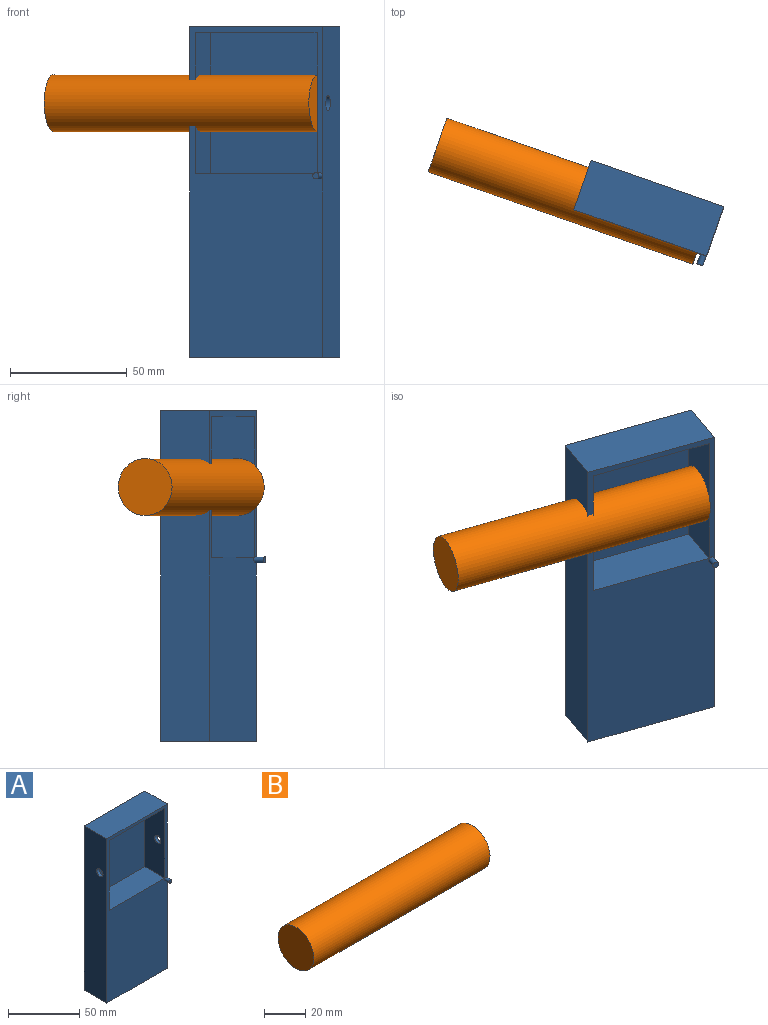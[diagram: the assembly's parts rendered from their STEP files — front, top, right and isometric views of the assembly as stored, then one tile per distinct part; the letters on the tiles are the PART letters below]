
ASSEMBLY  parts=2 mates=1
PART A: 43 faces, bbox 60.3x26.8x141.5 mm
  f0: plane 141.5x60.26mm, normal (0,-1,0), area 5197.6mm2, adj f1,f2,f3,f5,f6,f7,f8,f12
  f1: plane 141.5x22.41mm, normal (1,0,0), area 3139.2mm2, adj f0,f2,f4,f11,f39
  f2: plane 60.26x22.41mm, normal (0,0,1), area 1350.3mm2, adj f0,f1,f3,f4
  f3: plane 141.5x22.41mm, normal (-1,0,0), area 3139.2mm2, adj f0,f2,f4,f10,f39
  f4: plane 141.5x60.26mm, normal (0,1,0), area 8526.4mm2, adj f1,f2,f3,f39
  f5: plane 60.22x19.87mm, normal (-1,0,0), area 1164.8mm2, adj f0,f6,f8,f9,f11
  f6: plane 55.18x19.87mm, normal (0,0,-1), area 1096.3mm2, adj f0,f5,f7,f9
  f7: plane 60.22x19.87mm, normal (1,0,0), area 1164.8mm2, adj f0,f6,f8,f9,f10
  f8: plane 55.18x19.87mm, normal (0,0,1), area 1096.3mm2, adj f0,f5,f7,f9
  f9: plane 60.22x55.18mm, normal (0,-1,0), area 3322.8mm2, adj f5,f6,f7,f8
  f10: cylinder r=3.17mm len=6.35mm, axis (-1,0,0), area 50.7mm2, adj f3,f7
  f11: cylinder r=3.17mm len=6.35mm, axis (-1,0,0), area 50.7mm2, adj f1,f5
  f12: cylinder r=1.38mm len=4.42mm, axis (0,1,0), area 38.3mm2, adj f0,f13
  f13: plane 2.76x2.76mm, normal (0,-1,0), area 6mm2, adj f12
  f14: plane 76.2x3.35mm, normal (-0.94,0.34,0), area 271.5mm2, adj f15,f36,f39,f40
  f15: plane 76.2x1.5mm, normal (0,-1,0), area 114.7mm2, adj f14,f16,f39,f40
  f16: plane 76.2x2.47mm, normal (0.95,-0.3,0), area 197.2mm2, adj f15,f17,f39,f40
  f17: plane 76.2x2.47mm, normal (-0.81,-0.59,0), area 232.7mm2, adj f16,f18,f39,f40
  f18: plane 76.2x1.55mm, normal (0,-1,0), area 118.4mm2, adj f17,f19,f39,f40
  f19: plane 76.2x3.47mm, normal (0.8,0.6,0), area 331.3mm2, adj f18,f20,f39,f40
  f20: plane 76.2x3.17mm, normal (0.95,-0.32,0), area 255.2mm2, adj f19,f21,f39,f40
  f21: plane 76.2x1.45mm, normal (0,1,0), area 110.8mm2, adj f20,f22,f39,f40
  f22: plane 76.2x2.35mm, normal (-0.96,0.28,0), area 187mm2, adj f21,f23,f39,f40
  f23: plane 76.2x2.35mm, normal (0.82,0.57,0), area 219mm2, adj f22,f24,f39,f40
  f24: plane 76.2x1.56mm, normal (0,1,0), area 119.1mm2, adj f23,f36,f39,f40
  f25: plane 76.2x0.35mm, normal (0,-1,0), area 27mm2, adj f26,f37,f39,f41
  f26: plane 76.2x1.79mm, normal (0.98,0.21,0), area 139.8mm2, adj f25,f27,f39,f41
  f27: plane 76.2x0.34mm, normal (0,1,0), area 25.6mm2, adj f26,f28,f39,f41
  f28: extruded ~76.2x0.68mm, area 54.8mm2, adj f27,f29,f39,f41
  f29: extruded ~76.2x0.56mm, area 47.1mm2, adj f28,f30,f39,f41
  f30: extruded ~76.2x0.79mm, area 67.8mm2, adj f29,f37,f39,f41
  f31: plane 76.2x1.59mm, normal (-1,0.07,0), area 121.5mm2, adj f32,f38,f39,f42
  f32: plane 76.2x1.51mm, normal (0,-1,0), area 115.2mm2, adj f31,f33,f39,f42
  f33: plane 76.2x1.75mm, normal (0.9,0.44,0), area 148.3mm2, adj f32,f34,f39,f42
  f34: extruded ~76.2x1.15mm, area 95.8mm2, adj f33,f35,f39,f42
  f35: plane 76.2x0.16mm, normal (-1,0,0), area 12.5mm2, adj f34,f38,f39,f42
  f36: plane 76.2x3.29mm, normal (-0.8,-0.6,0), area 314mm2, adj f14,f24,f39,f40
  f37: extruded ~76.2x0.93mm, area 74.7mm2, adj f25,f30,f39,f41
  f38: extruded ~76.2x1.15mm, area 87.6mm2, adj f31,f35,f39,f42
  f39: plane 60.26x22.41mm, normal (0,0,-1), area 1327.6mm2, adj f0,f1,f3,f4,f14,f15,f16,f17
  f40: plane 6.9x6.64mm, normal (0,0,-1), area 18.4mm2, adj f14,f15,f16,f17,f18,f19,f20,f21
  f41: plane 1.79x1.61mm, normal (0,0,-1), area 2.2mm2, adj f25,f26,f27,f28,f29,f30,f37
  f42: plane 2.9x1.51mm, normal (0,0,-1), area 2.1mm2, adj f31,f32,f33,f34,f35,f38
PART B: 3 faces, bbox 120.1x24.4x24.4 mm
  f0: cylinder r=12.21mm len=120.13mm, axis (-1,0,0), area 9216mm2, adj f1,f2
  f1: plane 24.42x24.42mm, normal (1,0,0), area 468.3mm2, adj f0
  f2: plane 24.42x24.42mm, normal (-1,0,0), area 468.3mm2, adj f0
PLACE A rot(axis=(0,0,-1),19.2deg) t=(-2.65,-115.2,80.77)mm
PLACE B rot(axis=(0,0,-1),19.2deg) t=(-85.1,-102.83,83.58)mm
MATE cylindrical B.f0 <-> A.f10  axis (-0.94,0.33,0) through (-28.38,-122.58,83.58)mm
